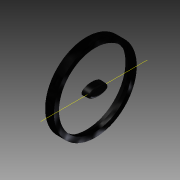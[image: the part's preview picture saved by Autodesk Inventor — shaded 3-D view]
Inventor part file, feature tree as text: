
AUTODESK INVENTOR PART (.ipt)
format: ipt  version: 2016 (Build 200138000, 138)  size: 658,944 bytes
history: native  units: in
note: dims shown in document units (in); Inventor stores cm internally (conversion verified against a paired STEP export)
features: sketch x23, extrude x17, plane x9, projected_geometry x5, loft x4, other x4, mirror x1, emboss x1, fillet x1
ambient origin geometry x8: Origin, YZ Plane, XZ Plane, XY Plane, X Axis, Y Axis, Z Axis, Center Point
bodies: Solid1 (feature_tree)
feature tree (65):
  sketch  "Sketch1"  dims[d0=0.7559in d1=0.7559in]
  plane  "Work Plane1"
  loft  "Loft1"
  extrude  "Extrusion1"  Depth=0.2in
  plane  "Work Plane4"
  loft  "Loft2"
  plane  "Work Plane5"
  loft  "Loft3"
  loft  "Loft4"
  extrude  "Extrusion2"  TaperAngle=0.0deg  [1 undecoded]
  plane  "Work Plane6"
  extrude  "Extrusion3"  Depth=1.0in
  extrude  "Extrusion4"  Depth=1.0651in
  extrude  "Extrusion5"  Depth=0.962in
  plane  "Work Plane7"
  extrude  "Extrusion6"  Depth=0.075in
  plane  "Work Plane8"
  other  "Work Axis1"
  plane  "Work Plane9"
  extrude  "Extrusion7"  Depth=0.06in
  mirror  "Mirror3"
  extrude  "Extrusion8"  Depth=0.05in
  plane  "Work Plane10"
  extrude  "Extrusion9"  Depth=0.0625in
  plane  "Work Plane11"
  extrude  "Extrusion10"  Depth=0.075in
  extrude  "Extrusion11"  TaperAngle=0.0deg  [1 undecoded]
  extrude  "Extrusion12"  Depth=0.2in
  extrude  "Extrusion13"  TaperAngle=0.0deg  [1 undecoded]
  emboss  "Emboss1"
  extrude  "Extrusion16"  Depth=0.01in
  extrude  "Extrusion17"  Depth=0.0344in
  extrude  "Extrusion18"  TaperAngle=60.0deg  [1 undecoded]
  fillet  "Fillet1"  [1 undecoded]
  extrude  "Extrusion20"  Depth=0.05in
  other  "Work Axis3"
  sketch  "Sketch2"  dims[d2=0.9963in d3=0.2in]
  sketch  "Sketch3"  dims[d4=0.5in d6=0.08in]
  sketch  "Sketch4"  dims[d7=0.55in d8=150.0deg]
  other  "Edges1"
  sketch  "Sketch5"  dims[d9=150.0deg d14=0.33in]
  projected_geometry  "Projected Loop1"
  other  "Edges2"
  sketch  "Sketch6"  dims[d15=0.66in d18=0.0in d19=90.0deg]
  sketch  "Sketch7"  dims[d20=0.0in d21=90.0deg d22=1.0in]
  sketch  "Sketch8"  dims[d26=1.0651in d28=1.0651in]
  sketch  "Sketch9"  dims[d29=0.0in d30=0.962in]
  sketch  "Sketch10"  dims[d31=0.962in d32=0.075in]
  sketch  "Sketch11"  dims[d33=0.15in d34=0.06in]
  sketch  "Sketch12"  dims[d35=0.1in d36=0.05in]
  sketch  "Sketch13"  dims[d37=0.45in d38=0.0in d39=0.0625in]
  projected_geometry  "Projected Loop2"
  projected_geometry  "Projected Loop3"
  sketch  "Sketch14"  dims[d40=0.01in d41=0.075in]
  projected_geometry  "Projected Loop4"
  sketch  "Sketch15"  dims[d42=0.01in d43=0.0in d44=90.0deg]
  sketch  "Sketch16"  dims[d45=0.0in d46=90.0deg d47=0.2in]
  sketch  "Sketch17"  dims[d48=0.07in d49=0.0in d50=90.0deg]
  sketch  "Sketch18"  dims[d51=0.0in d52=90.0deg d53=0.01in]
  sketch  "Sketch19"  dims[d54=0.01in d55=0.0344in]
  sketch  "Sketch23"  dims[d56=150.0deg d57=60.0deg d58=150.0deg]
  projected_geometry  "Projected Loop6"
  sketch  "Sketch24"  dims[d59=0.7in d60=0.05in]
  sketch  "Sketch25"  dims[d61=0.05in d62=0.05in]
  sketch  "Sketch27"  dims[d63=0.05in d64=0.05in d65=0.01in d66=0.0in d67=90.0deg d68=0.0in d69=90.0deg d70=0.1in d71=0.4in d72=0.15in d73=0.05in d74=0.0in d75=0.02in d77=0.15in d78=0.02in d79=0.1in d80=0.1in d81=0.1in d82=0.02in d83=0.15in d84=0.05in d85=0.0in d86=0.045in d87=0.0in d88=0.025in d89=0.0in d90=0.02in d91=0.02in d92=0.005in d93=0.0in d94=90.0deg d95=0.4466in d96=1.0in d97=0.0in d98=1.0in d99=0.0in d100=0.6528in d101=0.0in d102=0.0in d103=1.0in d104=0.0in d106=90.0deg d107=1.0in d108=0.0in d109=1.65in d110=0.1in d111=0.1in d112=0.0in d113=0.1in d114=0.075in d115=0.0in d116=0.05in d117=0.0in d123=0.84in d124=0.8in d125=0.0in d126=0.0in d127=1.0in d128=0.0in d130=0.15in d131=-0.0206in d135=0.2in d136=0.05in d137=0.1in d140=0.05in d141=0.1in d142=0.0in]
note: 5 required parameter values undecoded (feature->parameter linkage not recoverable at this tier; creation-order binding heuristic only, values carry confidence <= 0.55)
